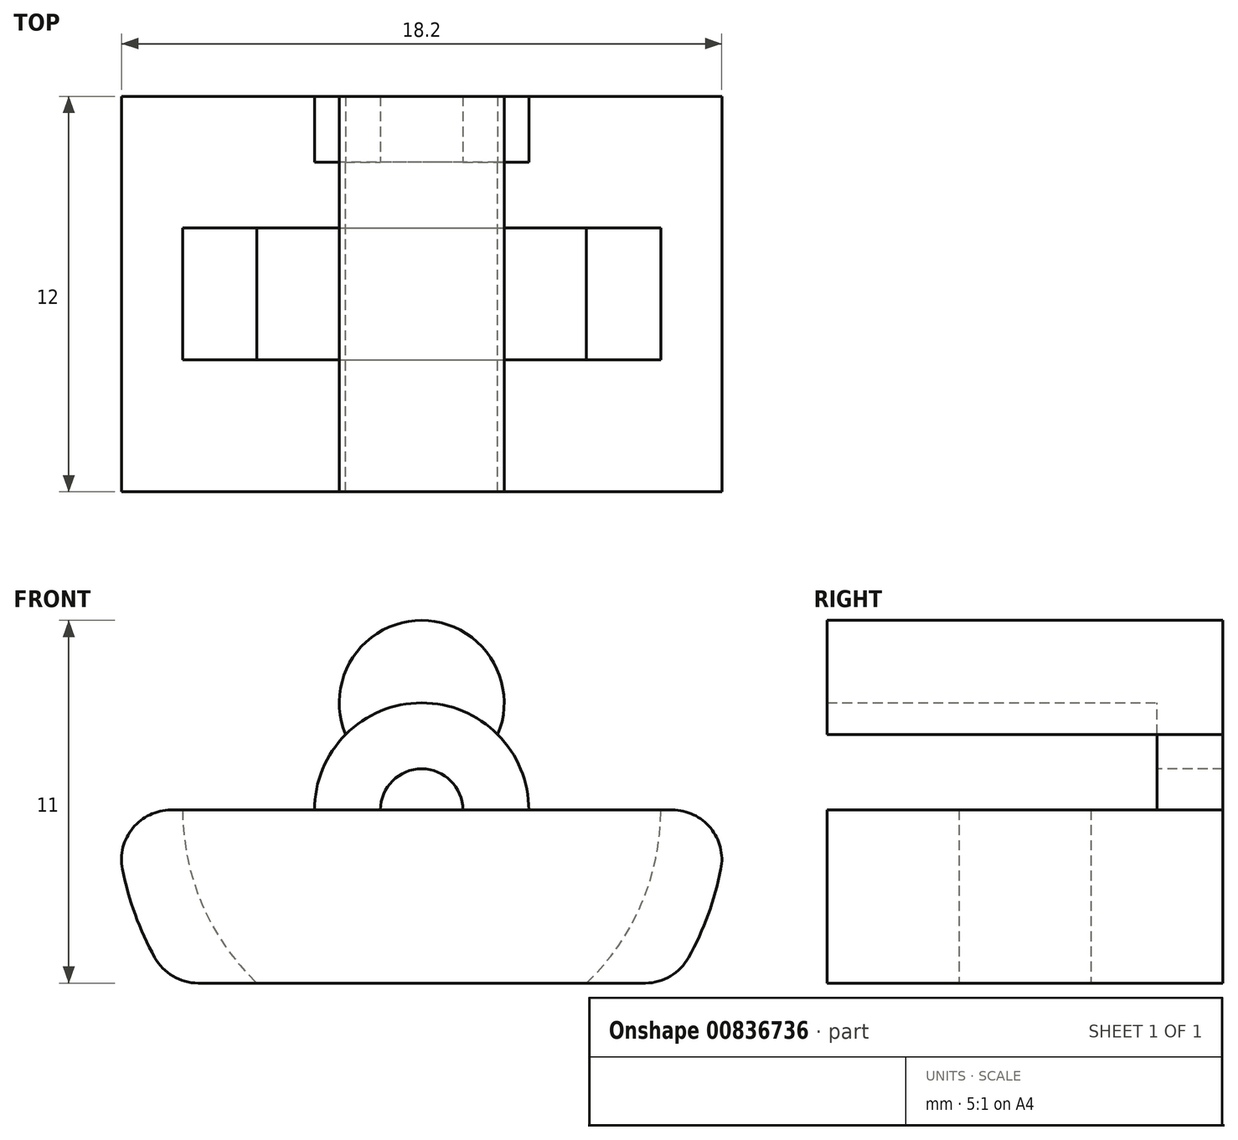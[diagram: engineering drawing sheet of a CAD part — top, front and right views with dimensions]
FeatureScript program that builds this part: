
annotation { "Feature Type Name" : "Feature", "Feature Type Description" : "" }
export const myFeature = defineFeature(function(context is Context, id is Id, definition is map)
    precondition{}
    {
        {
            var Q0;
            Q0=qCreatedBy(makeId("Front.planeOp"),FACE);
            var sketch = newSketch(context, id + "F0", { "sketchPlane" : qUnion([Q0])});
            skCircle(sketch, "E0", {"center": v(0, 0) * mm, "radius": 2.5 * mm});
            skCircle(sketch, "E1", {"center": v(0, -3.25) * mm, "radius": 5.25 * mm});
            skPoint(sketch, "E2", {"position": v(0, 2.5) * mm});
            skPoint(sketch, "E3", {"position": v(0, 2) * mm});
            skCircle(sketch, "E4", {"center": v(0, -3.25) * mm, "radius": 3.25 * mm});
            skCircle(sketch, "E5", {"center": v(0, -3.25) * mm, "radius": 1.25 * mm});
            skSolve(sketch);
        }
        {
            var Q0;
            {var subQ0=sQuery(id+"F0.wireOp",EDGE,"E1");var subQ1=sQuery(id+"F0.wireOp",EDGE,"E0");var subQ2=makeQuery(id+"F0.imprint","INTERSECT",VERTEX,{"disambiguationData":[OD(0.0)],"derivedFrom":[subQ1,subQ0]});Q0=makeQuery(id+"F0.imprint","IMPRINT",FACE,{"disambiguationData":[TD([[makeQuery(id+"F0.imprint","IMPRINT",EDGE,{"disambiguationData":[TD([[subQ2,-1.0]])],"derivedFrom":subQ1}),-1.0]])]});}
            var Q1;
            {var subQ0=sQuery(id+"F0.wireOp",EDGE,"E1");var subQ1=sQuery(id+"F0.wireOp",EDGE,"E0");var subQ2=makeQuery(id+"F0.imprint","INTERSECT",VERTEX,{"disambiguationData":[OD(0.0)],"derivedFrom":[subQ1,subQ0]});Q1=makeQuery(id+"F0.imprint","IMPRINT",FACE,{"disambiguationData":[TD([[makeQuery(id+"F0.imprint","IMPRINT",EDGE,{"disambiguationData":[TD([[subQ2,-1.0]])],"derivedFrom":subQ1}),1.0]])]});}
            var Q2;
            {var subQ0=sQuery(id+"F0.wireOp",EDGE,"E1");var subQ1=sQuery(id+"F0.wireOp",EDGE,"E0");var subQ2=makeQuery(id+"F0.imprint","INTERSECT",VERTEX,{"disambiguationData":[OD(0.0)],"derivedFrom":[subQ1,subQ0]});Q2=makeQuery(id+"F0.imprint","IMPRINT",FACE,{"disambiguationData":[TD([[makeQuery(id+"F0.imprint","IMPRINT",EDGE,{"disambiguationData":[TD([[subQ2,1.0]])],"derivedFrom":subQ1}),1.0]])]});}
            extrude(context, id + "F1", {"entities" : qUnion([Q0, Q1, Q2]), "depth" : 10 * mm, "offsetDistance" : 25 * mm});
        }
        {
            var Q0;
            Q0=makeQuery(id+"F0.imprint","IMPRINT",FACE,{"disambiguationData":[TD([[makeQuery(id+"F0.imprint","IMPRINT",EDGE,{"derivedFrom":sQuery(id+"F0.wireOp",EDGE,"E5")}),-1.0]])]});
            var Q1;
            {var subQ0=sQuery(id+"F0.wireOp",EDGE,"E4");var subQ1=sQuery(id+"F0.wireOp",EDGE,"E0");var subQ2=makeQuery(id+"F0.imprint","INTERSECT",VERTEX,{"disambiguationData":[OD(0.0)],"derivedFrom":[subQ1,subQ0]});Q1=makeQuery(id+"F0.imprint","IMPRINT",FACE,{"disambiguationData":[TD([[makeQuery(id+"F0.imprint","IMPRINT",EDGE,{"disambiguationData":[TD([[subQ2,-1.0]])],"derivedFrom":subQ1}),1.0]])]});}
            var Q2;
            {var subQ0=sQuery(id+"F0.wireOp",EDGE,"E1");var subQ1=sQuery(id+"F0.wireOp",EDGE,"E0");var subQ2=makeQuery(id+"F0.imprint","INTERSECT",VERTEX,{"disambiguationData":[OD(0.0)],"derivedFrom":[subQ1,subQ0]});Q2=makeQuery(id+"F0.imprint","IMPRINT",FACE,{"disambiguationData":[TD([[makeQuery(id+"F0.imprint","IMPRINT",EDGE,{"disambiguationData":[TD([[subQ2,-1.0]])],"derivedFrom":subQ1}),-1.0]])]});}
            var Q3;
            {var subQ0=sQuery(id+"F0.wireOp",EDGE,"E1");var subQ1=sQuery(id+"F0.wireOp",EDGE,"E0");var subQ2=makeQuery(id+"F0.imprint","INTERSECT",VERTEX,{"disambiguationData":[OD(0.0)],"derivedFrom":[subQ1,subQ0]});Q3=makeQuery(id+"F0.imprint","IMPRINT",FACE,{"disambiguationData":[TD([[makeQuery(id+"F0.imprint","IMPRINT",EDGE,{"disambiguationData":[TD([[subQ2,-1.0]])],"derivedFrom":subQ1}),1.0]])]});}
            var Q4;
            {var subQ0=sQuery(id+"F0.wireOp",EDGE,"E1");var subQ1=sQuery(id+"F0.wireOp",EDGE,"E0");var subQ2=makeQuery(id+"F0.imprint","INTERSECT",VERTEX,{"disambiguationData":[OD(0.0)],"derivedFrom":[subQ1,subQ0]});Q4=makeQuery(id+"F0.imprint","IMPRINT",FACE,{"disambiguationData":[TD([[makeQuery(id+"F0.imprint","IMPRINT",EDGE,{"disambiguationData":[TD([[subQ2,1.0]])],"derivedFrom":subQ1}),1.0]])]});}
            extrude(context, id + "F2", {"entities" : qUnion([Q0, Q1, Q2, Q3, Q4]), "operationType" : NewBodyOperationType.ADD, "oppositeDirection" : true, "depth" : 2 * mm, "offsetDistance" : 25 * mm});
        }
        {
            var Q0;
            Q0=makeQuery(id+"F1.opExtrude","CAP_FACE",FACE,{"disambiguationData":[OSD([sQuery(id+"F0.wireOp",EDGE,"E0"),sQuery(id+"F0.wireOp",EDGE,"E1"),sQuery(id+"F0.wireOp",EDGE,"E4")])],"isStart":false});
            var sketch = newSketch(context, id + "F3", { "sketchPlane" : qUnion([Q0])});
            skCircle(sketch, "E6", {"center": v(0, -3.25) * mm, "radius": 7.25 * mm});
            skCircle(sketch, "E7", {"center": v(0, -3.25) * mm, "radius": 9.25 * mm});
            skLineSegment(sketch, "E8", {"start": v(-7.62, -8.5) * mm, "end": v(7.62, -8.5) * mm});
            skPoint(sketch, "E8.startSnap0", {"position": v(0, -8.5) * mm});
            skLineSegment(sketch, "E9", {"start": v(-9.25, -3.25) * mm, "end": v(9.25, -3.25) * mm});
            skSolve(sketch);
        }
        {
            var Q0;
            {var subQ0=sQuery(id+"F3.wireOp",EDGE,"E9");var subQ1=sQuery(id+"F3.wireOp",EDGE,"E6");var subQ2=makeQuery(id+"F3.imprint","INTERSECT",VERTEX,{"disambiguationData":[OD(0.0)],"derivedFrom":[subQ1,subQ0]});Q0=makeQuery(id+"F3.imprint","IMPRINT",FACE,{"disambiguationData":[TD([[makeQuery(id+"F3.imprint","IMPRINT",EDGE,{"disambiguationData":[TD([[subQ2,-1.0]])],"derivedFrom":subQ1}),-1.0]])]});}
            var Q1;
            {var subQ0=sQuery(id+"F3.wireOp",EDGE,"E9");var subQ1=sQuery(id+"F3.wireOp",EDGE,"E6");var subQ2=makeQuery(id+"F3.imprint","INTERSECT",VERTEX,{"disambiguationData":[OD(0.0)],"derivedFrom":[subQ1,subQ0]});Q1=makeQuery(id+"F3.imprint","IMPRINT",FACE,{"disambiguationData":[TD([[makeQuery(id+"F3.imprint","IMPRINT",EDGE,{"disambiguationData":[TD([[subQ2,-1.0]])],"derivedFrom":subQ1}),1.0]])]});}
            var Q2;
            {var subQ0=sQuery(id+"F3.wireOp",EDGE,"E9");var subQ1=sQuery(id+"F3.wireOp",EDGE,"E6");var subQ2=makeQuery(id+"F3.imprint","INTERSECT",VERTEX,{"disambiguationData":[OD(1.0)],"derivedFrom":[subQ1,subQ0]});Q2=makeQuery(id+"F3.imprint","IMPRINT",FACE,{"disambiguationData":[TD([[makeQuery(id+"F3.imprint","IMPRINT",EDGE,{"disambiguationData":[TD([[subQ2,1.0]])],"derivedFrom":subQ1}),1.0]])]});}
            var Q3;
            {var subQ0=sQuery(id+"F3.wireOp",EDGE,"E9");var subQ1=sQuery(id+"F3.wireOp",EDGE,"E6");var subQ2=makeQuery(id+"F3.imprint","INTERSECT",VERTEX,{"disambiguationData":[OD(1.0)],"derivedFrom":[subQ1,subQ0]});Q3=makeQuery(id+"F3.imprint","IMPRINT",FACE,{"disambiguationData":[TD([[makeQuery(id+"F3.imprint","IMPRINT",EDGE,{"disambiguationData":[TD([[subQ2,1.0]])],"derivedFrom":subQ1}),-1.0]])]});}
            var Q4;
            Q4=makeQuery(id+"F2.opExtrude","CAP_FACE",FACE,{"disambiguationData":[OSD([sQuery(id+"F0.wireOp",EDGE,"E0"),sQuery(id+"F0.wireOp",EDGE,"E1"),sQuery(id+"F0.wireOp",EDGE,"E5")])],"isStart":false});
            extrude(context, id + "F4", {"entities" : qUnion([Q0, Q1, Q2, Q3]), "operationType" : NewBodyOperationType.ADD, "endBound" : BoundingType.UP_TO_SURFACE, "oppositeDirection" : true, "depth" : 25 * mm, "endBoundEntityFace" : qUnion([Q4]), "offsetDistance" : 25 * mm});
        }
        {
            var Q0;
            {var subQ0=sQuery(id+"F3.wireOp",EDGE,"E9");var subQ1=sQuery(id+"F3.wireOp",EDGE,"E6");var subQ2=makeQuery(id+"F3.imprint","INTERSECT",VERTEX,{"disambiguationData":[OD(1.0)],"derivedFrom":[subQ1,subQ0]});Q0=makeQuery(id+"F3.imprint","IMPRINT",FACE,{"disambiguationData":[TD([[makeQuery(id+"F3.imprint","IMPRINT",EDGE,{"disambiguationData":[TD([[subQ2,1.0]])],"derivedFrom":subQ1}),1.0]])]});}
            var Q1;
            {var subQ0=sQuery(id+"F3.wireOp",EDGE,"E9");var subQ1=sQuery(id+"F3.wireOp",EDGE,"E6");var subQ2=makeQuery(id+"F3.imprint","INTERSECT",VERTEX,{"disambiguationData":[OD(0.0)],"derivedFrom":[subQ1,subQ0]});Q1=makeQuery(id+"F3.imprint","IMPRINT",FACE,{"disambiguationData":[TD([[makeQuery(id+"F3.imprint","IMPRINT",EDGE,{"disambiguationData":[TD([[subQ2,-1.0]])],"derivedFrom":subQ1}),1.0]])]});}
            extrude(context, id + "F5", {"entities" : qUnion([Q0, Q1]), "operationType" : NewBodyOperationType.REMOVE, "oppositeDirection" : true, "depth" : 8 * mm, "offsetDistance" : 25 * mm, "hasSecondDirection" : true, "secondDirectionOppositeDirection" : true, "secondDirectionDepth" : 4 * mm});
        }
        {
            var Q0;
            {var subQ0=sQuery(id+"F3.wireOp",EDGE,"E9");var subQ1=sQuery(id+"F3.wireOp",EDGE,"E7");Q0=makeQuery(id+"F4.opExtrude","SWEPT_EDGE",EDGE,{"disambiguationData":[OSD([subQ1,subQ0]),TDD([makeQuery(id+"F3.imprint","INTERSECT",VERTEX,{"disambiguationData":[OD(0.0)],"derivedFrom":[subQ1,subQ0]})])]});}
            var Q1;
            {var subQ0=sQuery(id+"F3.wireOp",EDGE,"E9");var subQ1=sQuery(id+"F3.wireOp",EDGE,"E7");Q1=makeQuery(id+"F4.opExtrude","SWEPT_EDGE",EDGE,{"disambiguationData":[OSD([subQ1,subQ0]),TDD([makeQuery(id+"F3.imprint","INTERSECT",VERTEX,{"disambiguationData":[OD(1.0)],"derivedFrom":[subQ1,subQ0]})])]});}
            var Q2;
            {var subQ0=sQuery(id+"F3.wireOp",EDGE,"E8");var subQ1=sQuery(id+"F3.wireOp",EDGE,"E7");Q2=makeQuery(id+"F4.opExtrude","SWEPT_EDGE",EDGE,{"disambiguationData":[OSD([subQ1,subQ0]),TDD([makeQuery(id+"F3.imprint","INTERSECT",VERTEX,{"disambiguationData":[OD(1.0)],"derivedFrom":[subQ1,subQ0]})])]});}
            var Q3;
            {var subQ0=sQuery(id+"F3.wireOp",EDGE,"E8");var subQ1=sQuery(id+"F3.wireOp",EDGE,"E7");Q3=makeQuery(id+"F4.opExtrude","SWEPT_EDGE",EDGE,{"disambiguationData":[OSD([subQ1,subQ0]),TDD([makeQuery(id+"F3.imprint","INTERSECT",VERTEX,{"disambiguationData":[OD(0.0)],"derivedFrom":[subQ1,subQ0]})])]});}
            var Q4;
            {var subQ1=sQuery(id+"F0.wireOp",EDGE,"E1");var subQ2=makeQuery(id+"F1.opExtrude","CAP_EDGE",EDGE,{"disambiguationData":[OSD([subQ1])],"isStart":false});var subQ4=sQuery(id+"F3.wireOp",EDGE,"E9");var subQ5=makeQuery(id+"F3.imprint","INTERSECT",VERTEX,{"disambiguationData":[OD(0.0)],"derivedFrom":[subQ2,subQ4]});Q4=makeQuery(id+"F5.boolean.opBoolean","SPLIT",EDGE,{"disambiguationData":[TD([makeQuery(id+"F1.opExtrude","CAP_FACE",FACE,{"disambiguationData":[OSD([sQuery(id+"F0.wireOp",EDGE,"E0"),subQ1,sQuery(id+"F0.wireOp",EDGE,"E4")])],"isStart":false})])],"derivedFrom":makeQuery(id+"F4.opExtrude","SWEPT_EDGE",EDGE,{"disambiguationData":[OSD([subQ1,subQ4]),TDD([subQ5])]})});}
            var Q5;
            {var subQ0=sQuery(id+"F3.wireOp",EDGE,"E9");var subQ3=sQuery(id+"F0.wireOp",EDGE,"E1");var subQ4=makeQuery(id+"F1.opExtrude","CAP_EDGE",EDGE,{"disambiguationData":[OSD([subQ3])],"isStart":false});var subQ5=makeQuery(id+"F3.imprint","INTERSECT",VERTEX,{"disambiguationData":[OD(0.0)],"derivedFrom":[subQ4,subQ0]});var subQ7=sQuery(id+"F0.wireOp",EDGE,"E5");var subQ8=sQuery(id+"F0.wireOp",EDGE,"E0");Q5=makeQuery(id+"F5.boolean.opBoolean","SPLIT",EDGE,{"disambiguationData":[TD([makeQuery(id+"F2.opExtrude","CAP_FACE",FACE,{"disambiguationData":[OSD([subQ8,subQ3,subQ7])],"isStart":false})])],"derivedFrom":makeQuery(id+"F4.opExtrude","SWEPT_EDGE",EDGE,{"disambiguationData":[OSD([subQ3,subQ0]),TDD([subQ5])]})});}
            var Q6;
            {var subQ1=sQuery(id+"F0.wireOp",EDGE,"E1");var subQ2=makeQuery(id+"F1.opExtrude","CAP_EDGE",EDGE,{"disambiguationData":[OSD([subQ1])],"isStart":false});var subQ4=sQuery(id+"F3.wireOp",EDGE,"E9");var subQ13=makeQuery(id+"F3.imprint","INTERSECT",VERTEX,{"disambiguationData":[OD(1.0)],"derivedFrom":[subQ2,subQ4]});Q6=makeQuery(id+"F5.boolean.opBoolean","SPLIT",EDGE,{"disambiguationData":[TD([makeQuery(id+"F1.opExtrude","CAP_FACE",FACE,{"disambiguationData":[OSD([sQuery(id+"F0.wireOp",EDGE,"E0"),subQ1,sQuery(id+"F0.wireOp",EDGE,"E4")])],"isStart":false})])],"derivedFrom":makeQuery(id+"F4.opExtrude","SWEPT_EDGE",EDGE,{"disambiguationData":[OSD([subQ1,subQ4]),TDD([subQ13])]})});}
            var Q7;
            {var subQ0=sQuery(id+"F3.wireOp",EDGE,"E9");var subQ3=sQuery(id+"F0.wireOp",EDGE,"E1");var subQ4=makeQuery(id+"F1.opExtrude","CAP_EDGE",EDGE,{"disambiguationData":[OSD([subQ3])],"isStart":false});var subQ5=makeQuery(id+"F3.imprint","INTERSECT",VERTEX,{"disambiguationData":[OD(1.0)],"derivedFrom":[subQ4,subQ0]});var subQ9=sQuery(id+"F0.wireOp",EDGE,"E5");var subQ10=sQuery(id+"F0.wireOp",EDGE,"E0");Q7=makeQuery(id+"F5.boolean.opBoolean","SPLIT",EDGE,{"disambiguationData":[TD([makeQuery(id+"F2.opExtrude","CAP_FACE",FACE,{"disambiguationData":[OSD([subQ10,subQ3,subQ9])],"isStart":false})])],"derivedFrom":makeQuery(id+"F4.opExtrude","SWEPT_EDGE",EDGE,{"disambiguationData":[OSD([subQ3,subQ0]),TDD([subQ5])]})});}
            fillet(context, id + "F6", {"entities" : qUnion([Q0, Q1, Q2, Q3, Q4, Q5, Q6, Q7]), "radius" : 1.5 * mm, "tangentPropagation" : true, "allowEdgeOverflow" : false});
        }
    });
